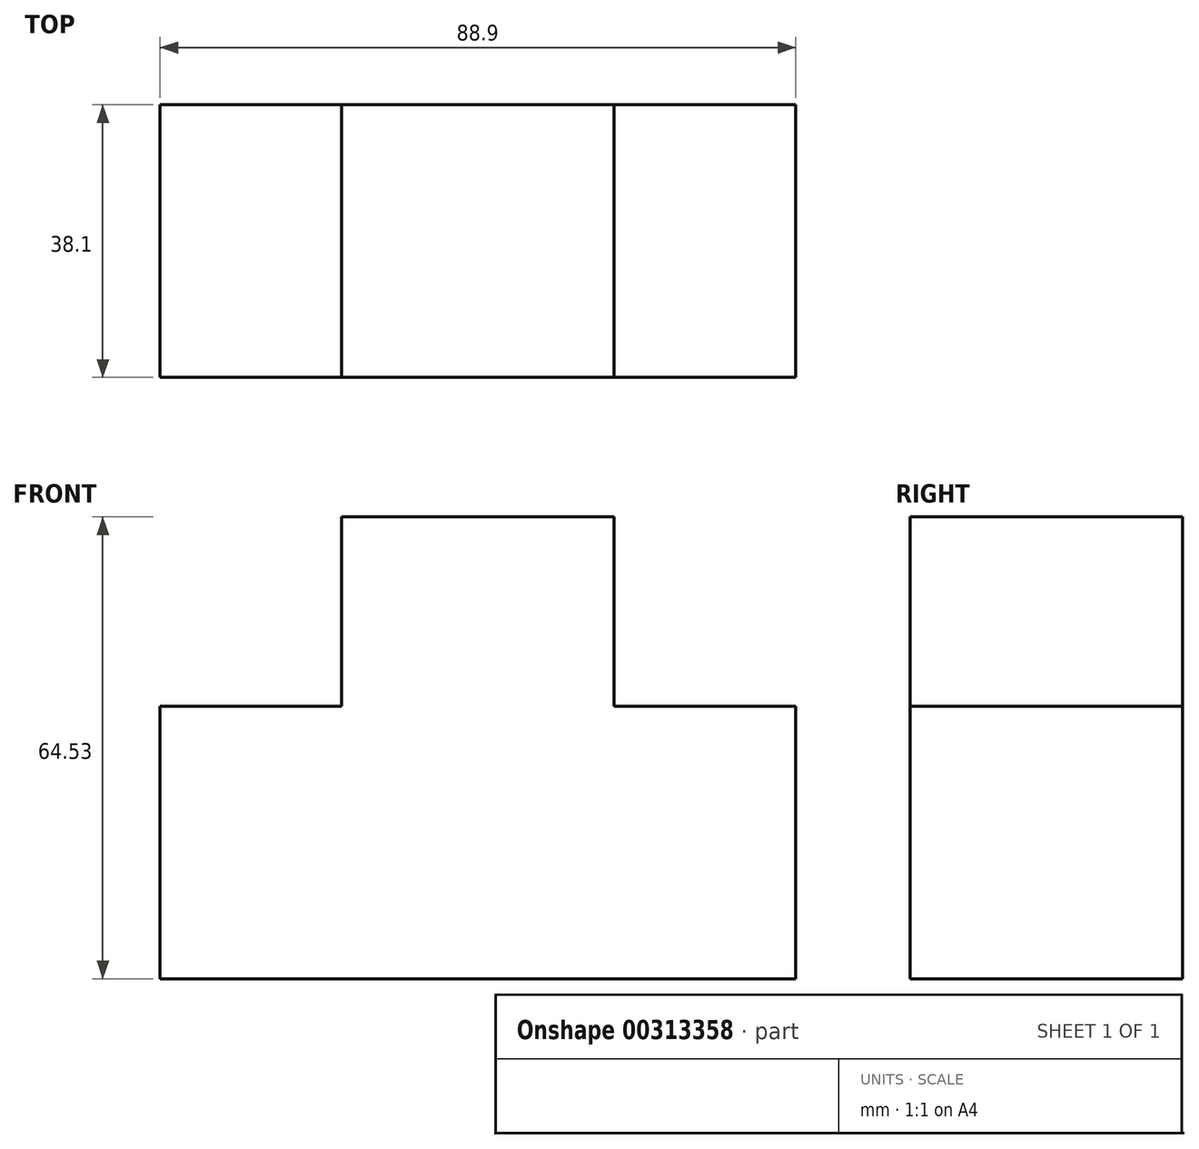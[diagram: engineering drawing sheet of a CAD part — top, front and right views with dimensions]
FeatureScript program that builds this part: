
annotation { "Feature Type Name" : "Feature", "Feature Type Description" : "" }
export const myFeature = defineFeature(function(context is Context, id is Id, definition is map)
    precondition{}
    {
        {
            var Q0;
            Q0=qCreatedBy(makeId("Front.planeOp"),FACE);
            var sketch = newSketch(context, id + "F0", { "sketchPlane" : qUnion([Q0])});
            skLineSegment(sketch, "E0", {"start": v(-37.5, -31.96) * mm, "end": v(51.4, -31.96) * mm});
            skLineSegment(sketch, "E1", {"start": v(51.4, -31.96) * mm, "end": v(51.4, 6.14) * mm});
            skLineSegment(sketch, "E2", {"start": v(51.4, 6.14) * mm, "end": v(26, 6.14) * mm});
            skLineSegment(sketch, "E3", {"start": v(26, 6.14) * mm, "end": v(26, 32.57) * mm});
            skLineSegment(sketch, "E4", {"start": v(26, 32.57) * mm, "end": v(-12.1, 32.57) * mm});
            skLineSegment(sketch, "E5", {"start": v(-12.1, 32.57) * mm, "end": v(-12.1, 6.14) * mm});
            skLineSegment(sketch, "E6", {"start": v(-12.1, 6.14) * mm, "end": v(-37.5, 6.14) * mm});
            skLineSegment(sketch, "E7", {"start": v(-37.5, 6.14) * mm, "end": v(-37.5, -31.96) * mm});
            skSolve(sketch);
        }
        {
            var Q0;
            Q0 = qSketchRegion(id + "F0", true);
            extrude(context, id + "F1", {"entities" : qUnion([Q0]), "depth" : 38.1 * mm});
        }
    });
